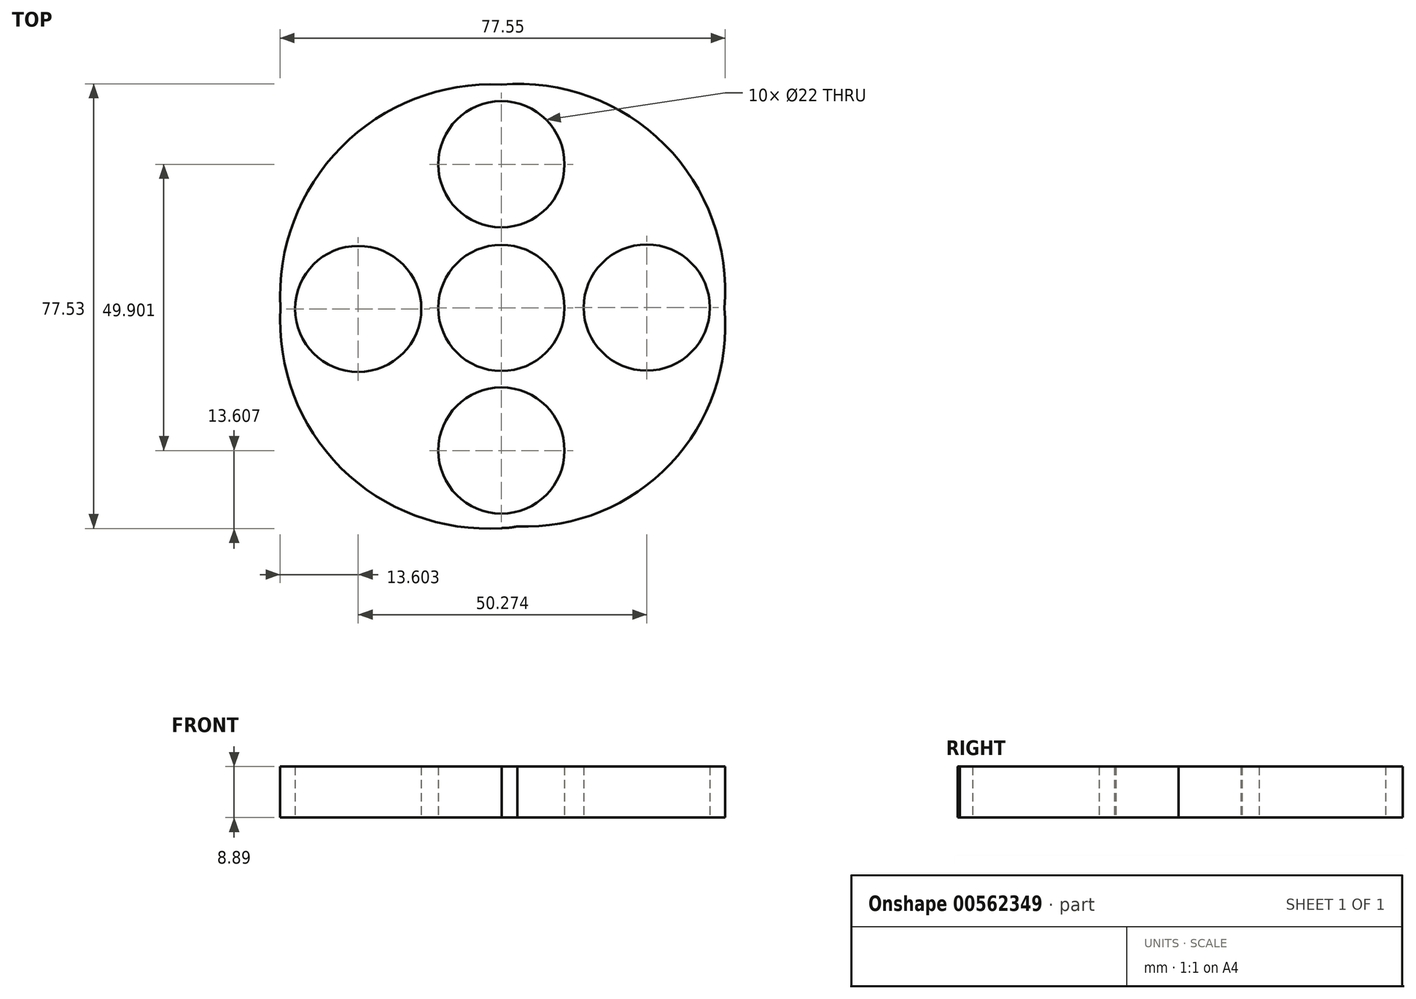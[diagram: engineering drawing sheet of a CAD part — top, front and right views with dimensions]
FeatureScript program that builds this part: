
annotation { "Feature Type Name" : "Feature", "Feature Type Description" : "" }
export const myFeature = defineFeature(function(context is Context, id is Id, definition is map)
    precondition{}
    {
        {
            var Q0;
            Q0=qCreatedBy(makeId("Top.planeOp"),FACE);
            var sketch = newSketch(context, id + "F0", { "sketchPlane" : qUnion([Q0])});
            skCircle(sketch, "E0", {"center": v(0, 0) * mm, "radius": 11 * mm});
            skCircle(sketch, "E1", {"center": v(0, 25.04) * mm, "radius": 11 * mm});
            skCircle(sketch, "E2", {"center": v(25.33, 0.06) * mm, "radius": 11 * mm});
            skCircle(sketch, "E3", {"center": v(-24.95, -0.18) * mm, "radius": 11 * mm});
            skCircle(sketch, "E4", {"center": v(0, 25.04) * mm, "radius": 13.9 * mm});
            skCircle(sketch, "E5", {"center": v(-24.95, -0.18) * mm, "radius": 13.53 * mm});
            skCircle(sketch, "E6", {"center": v(25.33, 0.06) * mm, "radius": 13.53 * mm});
            skCircle(sketch, "E7", {"center": v(0, -24.86) * mm, "radius": 11 * mm});
            skCircle(sketch, "E8", {"center": v(0, -24.86) * mm, "radius": 13.53 * mm});
            skArc(sketch, "E9", {"start": v(38.85, 0) * mm, "mid": v(28.45, 28.47) * mm, "end": v(0, 38.94) * mm});
            skArc(sketch, "E10", {"start": v(2.81, -38.1) * mm, "mid": v(29.45, -27.2) * mm, "end": v(38.85, 0) * mm});
            skArc(sketch, "E11", {"start": v(0, 38.94) * mm, "mid": v(-27.9, 28.03) * mm, "end": v(-38.47, 0) * mm});
            skArc(sketch, "E12", {"start": v(-38.47, 0) * mm, "mid": v(-26.9, -28.88) * mm, "end": v(2.81, -38.1) * mm});
            skSolve(sketch);
        }
        {
            var Q0;
            Q0 = qSketchRegion(id + "F0", true);
            extrude(context, id + "F1", {"entities" : qUnion([Q0]), "depth" : 8.9 * mm, "offsetDistance" : 25.4 * mm});
        }
    });
